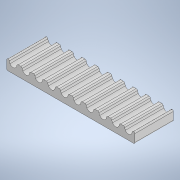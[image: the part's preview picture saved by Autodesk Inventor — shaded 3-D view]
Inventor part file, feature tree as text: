
AUTODESK INVENTOR PART (.ipt)
format: ipt  version: 2021 (Build 250183000, 183)  size: 207,360 bytes
history: native  units: mm
features: other x1, extrude x1, fillet x1, sketch x1
ambient origin geometry x8: Origin, YZ Plane, XZ Plane, XY Plane, X Axis, Y Axis, Z Axis, Center Point
bodies: Body1 (feature_tree)
feature tree (4):
  other  "ソリッド1"
  extrude  "押し出し1"  Depth=1.37mm
  fillet  "フィレット1"  Radius=2.54mm
  sketch  "スケッチ1"
